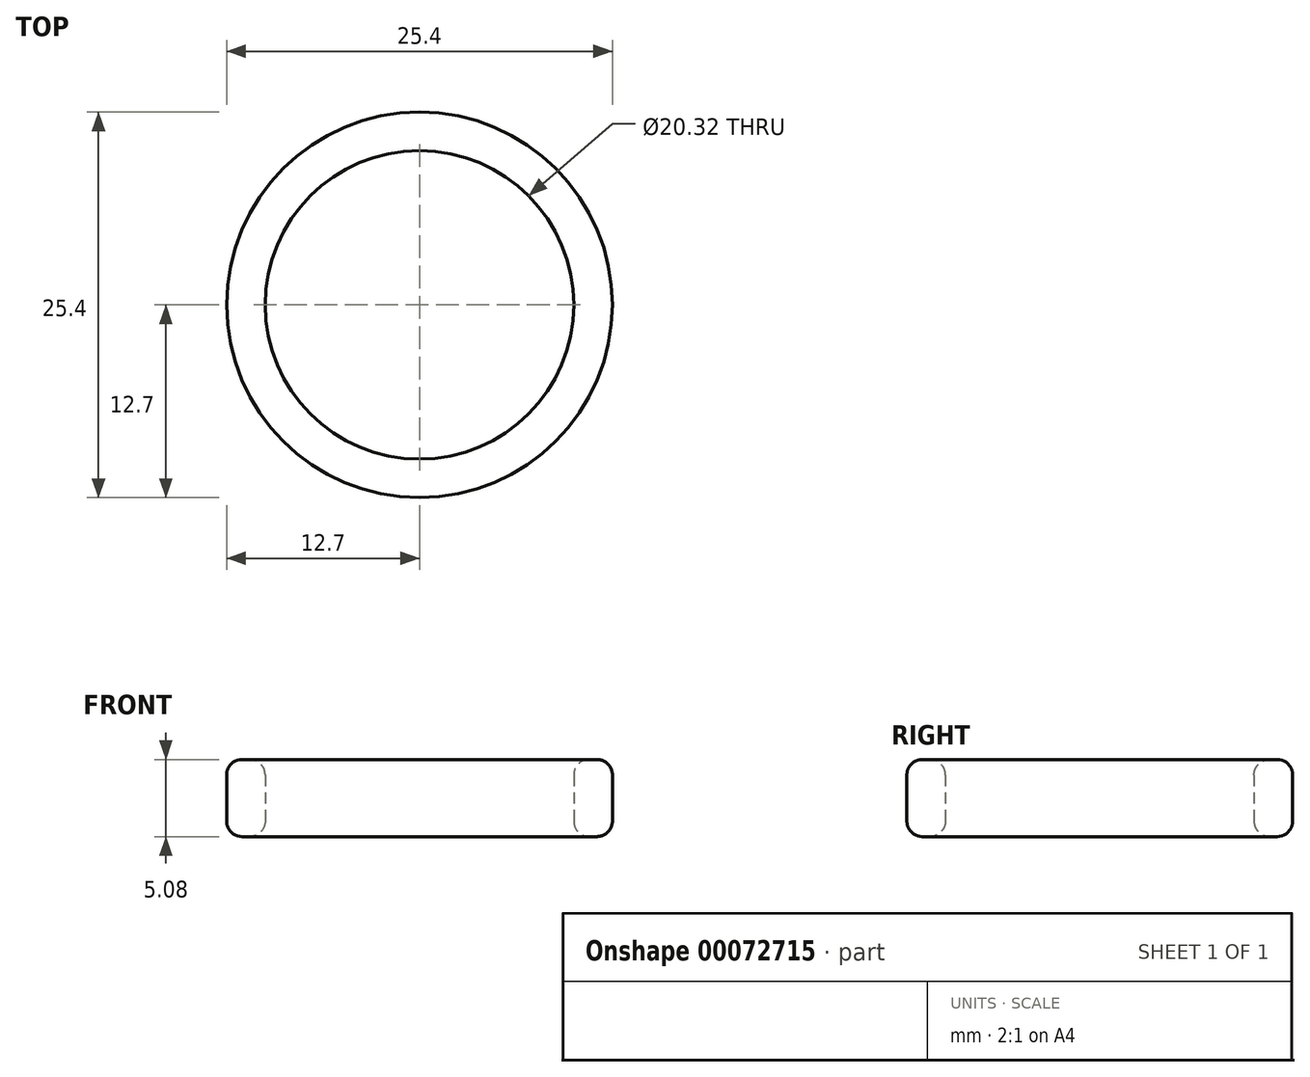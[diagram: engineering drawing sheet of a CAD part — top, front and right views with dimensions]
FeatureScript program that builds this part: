
annotation { "Feature Type Name" : "Feature", "Feature Type Description" : "" }
export const myFeature = defineFeature(function(context is Context, id is Id, definition is map)
    precondition{}
    {
        {
            var Q0;
            Q0=qCreatedBy(makeId("Top.planeOp"),FACE);
            var sketch = newSketch(context, id + "F0", { "sketchPlane" : qUnion([Q0])});
            skCircle(sketch, "E0", {"center": v(0, 0) * mm, "radius": 10.16 * mm});
            skCircle(sketch, "E1", {"center": v(0, 0) * mm, "radius": 12.7 * mm});
            skSolve(sketch);
        }
        {
            var Q0;
            Q0 = qSketchRegion(id + "F0", true);
            extrude(context, id + "F1", {"entities" : qUnion([Q0]), "depth" : 2.54 * mm, "hasSecondDirection" : true, "secondDirectionOppositeDirection" : true, "secondDirectionDepth" : 2.54 * mm});
        }
        {
            var Q0;
            Q0=makeQuery(id+"F1.opExtrude","SWEPT_FACE",FACE,{"disambiguationData":[OSD([sQuery(id+"F0.wireOp",EDGE,"E1")])]});
            var Q1;
            Q1=makeQuery(id+"F1.opExtrude","SWEPT_FACE",FACE,{"disambiguationData":[OSD([sQuery(id+"F0.wireOp",EDGE,"E0")])]});
            fillet(context, id + "F2", {"entities" : qUnion([Q0, Q1]), "radius" : 1.02 * mm, "tangentPropagation" : true, "allowEdgeOverflow" : false});
        }
    });
